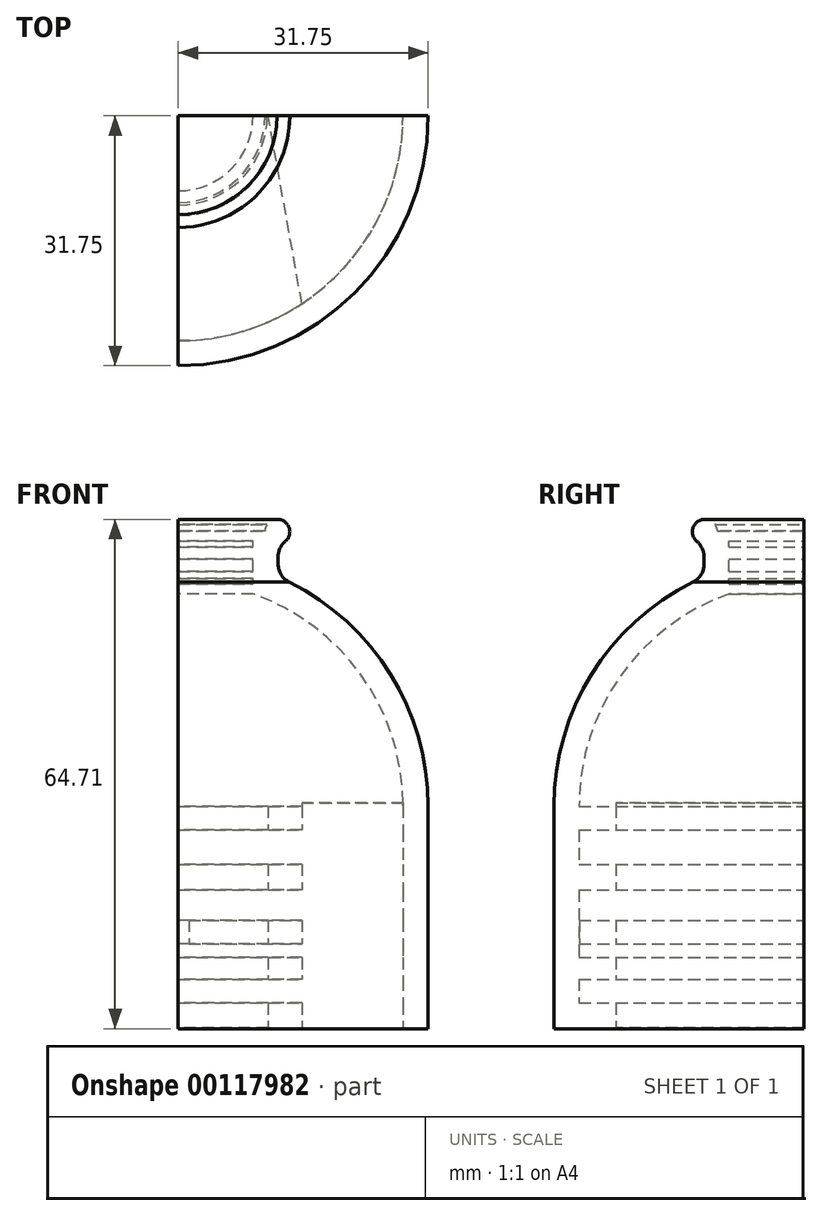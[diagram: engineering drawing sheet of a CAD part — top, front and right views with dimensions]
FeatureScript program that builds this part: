
annotation { "Feature Type Name" : "Feature", "Feature Type Description" : "" }
export const myFeature = defineFeature(function(context is Context, id is Id, definition is map)
    precondition{}
    {
        {
            var Q0;
            Q0=qCreatedBy(makeId("Top.planeOp"),FACE);
            var sketch = newSketch(context, id + "F0", { "sketchPlane" : qUnion([Q0])});
            skCircle(sketch, "E0", {"center": v(0, 0) * mm, "radius": 31.75 * mm});
            skCircle(sketch, "E1", {"center": v(0, 0) * mm, "radius": 28.58 * mm});
            skSolve(sketch);
        }
        {
            var Q0;
            Q0=qSketchRegion(id+"F0",true);
            extrude(context, id + "F1", {"entities" : qUnion([Q0]), "endBound" : BoundingType.SYMMETRIC, "depth" : 50.8 * mm});
        }
        {
            var Q0;
            Q0=makeQuery(id+"F1.opExtrude","CAP_FACE",FACE,{"disambiguationData":[OSD([sQuery(id+"F0.wireOp",EDGE,"E0"),sQuery(id+"F0.wireOp",EDGE,"E1")])],"isStart":false});
            var sketch = newSketch(context, id + "F2", { "sketchPlane" : qUnion([Q0])});
            skArc(sketch, "E2", {"start": v(0, -31.75) * mm, "mid": v(31.75, 0) * mm, "end": v(0, 31.75) * mm});
            skArc(sketch, "E3", {"start": v(0, -28.58) * mm, "mid": v(28.58, 0) * mm, "end": v(0, 28.58) * mm});
            skLineSegment(sketch, "E4", {"start": v(0, 31.75) * mm, "end": v(0, -31.75) * mm, "construction": true});
            skLineSegment(sketch, "E5", {"start": v(0, 31.75) * mm, "end": v(0, 28.58) * mm});
            skLineSegment(sketch, "E6", {"start": v(0, -31.75) * mm, "end": v(0, -28.58) * mm});
            skSolve(sketch);
        }
        {
            var Q0;
            Q0=qSketchRegion(id+"F2",true);
            var Q1;
            Q1=sQuery(id+"F2.wireOp",EDGE,"E4");
            revolve(context, id + "F3", {"operationType" : NewBodyOperationType.ADD, "entities" : qUnion([Q0]), "axis" : qUnion([Q1]), "revolveType" : RevolveType.ONE_DIRECTION, "angle" : 180 * degree});
        }
        {
            var Q0;
            Q0=makeQuery(id+"F1.opExtrude","SWEPT_BODY",BODY,{"disambiguationData":[OSD([sQuery(id+"F0.wireOp",EDGE,"E0"),sQuery(id+"F0.wireOp",EDGE,"E1")])]});
            var Q1;
            Q1=qCreatedBy(makeId("Top.planeOp"),FACE);
            mirror(context, id + "F4", {"operationType" : NewBodyOperationType.ADD, "entities" : qUnion([Q0]), "mirrorPlane" : qUnion([Q1])});
        }
        {
            var Q0;
            Q0=qCreatedBy(makeId("Top.planeOp"),FACE);
            cPlane(context, id + "F5", {"entities" : qUnion([Q0]), "cplaneType" : CPlaneType.OFFSET, "offset" : 57.15 * mm, "width" : 152.4 * mm, "height" : 152.4 * mm});
        }
        {
            var Q0;
            Q0=qCreatedBy(id+"F5.planeOp",FACE);
            var sketch = newSketch(context, id + "F6", { "sketchPlane" : qUnion([Q0])});
            skCircle(sketch, "E7", {"center": v(0, 0) * mm, "radius": 12.7 * mm});
            skSolve(sketch);
        }
        {
            var Q0;
            Q0=qSketchRegion(id+"F6",true);
            extrude(context, id + "F7", {"entities" : qUnion([Q0]), "operationType" : NewBodyOperationType.ADD, "endBound" : BoundingType.SYMMETRIC, "depth" : 6.35 * mm});
        }
        {
            var Q0;
            Q0=qCreatedBy(makeId("Top.planeOp"),FACE);
            cPlane(context, id + "F8", {"entities" : qUnion([Q0]), "cplaneType" : CPlaneType.OFFSET, "offset" : 57.15 * mm, "oppositeDirection" : true, "width" : 152.4 * mm, "height" : 152.4 * mm});
        }
        {
            var Q0;
            Q0=makeQuery(id+"F7.opExtrude","CAP_FACE",FACE,{"disambiguationData":[OSD([sQuery(id+"F6.wireOp",EDGE,"E7")])],"isStart":false});
            var sketch = newSketch(context, id + "F9", { "sketchPlane" : qUnion([Q0])});
            skCircle(sketch, "E8", {"center": v(0, 0) * mm, "radius": 9.53 * mm});
            skSolve(sketch);
        }
        {
            var Q0;
            Q0=qSketchRegion(id+"F9",true);
            extrude(context, id + "F10", {"entities" : qUnion([Q0]), "operationType" : NewBodyOperationType.REMOVE, "oppositeDirection" : true, "depth" : 25.4 * mm});
        }
        {
            var Q0;
            Q0=qCreatedBy(makeId("Front.planeOp"),FACE);
            var sketch = newSketch(context, id + "F11", { "sketchPlane" : qUnion([Q0])});
            skLineSegment(sketch, "E9", {"start": v(0, -57.15) * mm, "end": v(11.6, -79.09) * mm});
            skLineSegment(sketch, "E10", {"start": v(11.6, -79.09) * mm, "end": v(33.29, -79.09) * mm});
            skLineSegment(sketch, "E11", {"start": v(33.29, -79.09) * mm, "end": v(33.29, -57.05) * mm});
            skLineSegment(sketch, "E12", {"start": v(33.29, -57.05) * mm, "end": v(28.2, -40) * mm});
            skPoint(sketch, "E13.orphan", {"position": v(31.75, -25.4) * mm});
            skPoint(sketch, "E14.orphan", {"position": v(-31.75, -25.4) * mm});
            skLineSegment(sketch, "E15", {"start": v(28.2, -40) * mm, "end": v(27.19, -39.19) * mm});
            skArc(sketch, "E16.0", {"start": v(0, -56.61) * mm, "mid": v(14.18, -53.2) * mm, "end": v(25.27, -43.72) * mm});
            skLineSegment(sketch, "E17", {"start": v(27.19, -39.19) * mm, "end": v(25.27, -43.72) * mm});
            skLineSegment(sketch, "E18", {"start": v(0, -56.61) * mm, "end": v(0, -57.15) * mm});
            skSolve(sketch);
        }
        {
            var Q0;
            Q0=qSketchRegion(id+"F11",true);
            extrude(context, id + "F12", {"entities" : qUnion([Q0]), "operationType" : NewBodyOperationType.ADD, "endBound" : BoundingType.SYMMETRIC, "depth" : 3.17 * mm});
        }
        {
            var Q0;
            Q0=qCreatedBy(makeId("Front.planeOp"),FACE);
            var sketch = newSketch(context, id + "F13", { "sketchPlane" : qUnion([Q0])});
            skLineSegment(sketch, "E19", {"start": v(0, 72.95) * mm, "end": v(0, -20.55) * mm, "construction": true});
            skSolve(sketch);
        }
        {
            var Q0;
            Q0=makeQuery(id+"F1.opExtrude","SWEPT_BODY",BODY,{"disambiguationData":[OSD([sQuery(id+"F0.wireOp",EDGE,"E0"),sQuery(id+"F0.wireOp",EDGE,"E1")])]});
            var Q1;
            Q1=sQuery(id+"F13.wireOp",EDGE,"E19");
            circularPattern(context, id + "F14", {"entities" : qUnion([Q0]), "axis" : qUnion([Q1]), "angle" : 90 * degree, "instanceCount" : 4});
        }
        {
            var Q0;
            Q0=qCreatedBy(makeId("Front.planeOp"),FACE);
            var sketch = newSketch(context, id + "F15", { "sketchPlane" : qUnion([Q0])});
            skLineSegment(sketch, "E20", {"start": v(0, 46.85) * mm, "end": v(0, 31.4) * mm, "construction": true});
            skCircle(sketch, "E21", {"center": v(12.6, 60.23) * mm, "radius": 1.59 * mm});
            skSolve(sketch);
        }
        {
            var Q0;
            Q0=qSketchRegion(id+"F15",true);
            var Q1;
            Q1=sQuery(id+"F15.wireOp",EDGE,"E20");
            revolve(context, id + "F16", {"operationType" : NewBodyOperationType.ADD, "entities" : qUnion([Q0]), "axis" : qUnion([Q1]), "revolveType" : RevolveType.FULL});
        }
        {
            var Q0;
            Q0=qCreatedBy(id+"F5.planeOp",FACE);
            var sketch = newSketch(context, id + "F17", { "sketchPlane" : qUnion([Q0])});
            skLineSegment(sketch, "E22", {"start": v(0, -45.12) * mm, "end": v(0, 0) * mm});
            skLineSegment(sketch, "E23", {"start": v(0, 0) * mm, "end": v(39.38, 0) * mm});
            skLineSegment(sketch, "E24", {"start": v(39.38, 0) * mm, "end": v(39.38, 53.9) * mm});
            skLineSegment(sketch, "E25", {"start": v(39.38, 53.9) * mm, "end": v(-55.46, 53.9) * mm});
            skLineSegment(sketch, "E26", {"start": v(-55.46, 53.9) * mm, "end": v(-55.46, -47.21) * mm});
            skLineSegment(sketch, "E27", {"start": v(-55.46, -47.21) * mm, "end": v(0, -45.12) * mm});
            skSolve(sketch);
        }
        {
            var Q0;
            Q0=qSketchRegion(id+"F17",true);
            extrude(context, id + "F18", {"entities" : qUnion([Q0]), "operationType" : NewBodyOperationType.REMOVE, "endBound" : BoundingType.THROUGH_ALL, "oppositeDirection" : true, "depth" : 25.4 * mm, "hasSecondDirection" : true, "secondDirectionOppositeDirection" : false, "secondDirectionDepth" : 25.4 * mm});
        }
        {
            var Q0;
            Q0=qCreatedBy(makeId("Right.planeOp"),FACE);
            var sketch = newSketch(context, id + "F19", { "sketchPlane" : qUnion([Q0])});
            skLineSegment(sketch, "E28.bottom", {"start": v(8.43, -2.89) * mm, "end": v(-42.27, -2.89) * mm});
            skLineSegment(sketch, "E28.top", {"start": v(8.43, -82.1) * mm, "end": v(-42.27, -82.1) * mm});
            skLineSegment(sketch, "E28.left", {"start": v(8.43, -2.89) * mm, "end": v(8.43, -82.1) * mm});
            skLineSegment(sketch, "E28.right", {"start": v(-42.27, -2.89) * mm, "end": v(-42.27, -82.1) * mm});
            skSolve(sketch);
        }
        {
            var Q0;
            Q0=qSketchRegion(id+"F19",true);
            extrude(context, id + "F20", {"entities" : qUnion([Q0]), "operationType" : NewBodyOperationType.REMOVE, "endBound" : BoundingType.THROUGH_ALL, "depth" : 25.4 * mm});
        }
        {
            var Q0;
            Q0=qCreatedBy(makeId("Right.planeOp"),FACE);
            var sketch = newSketch(context, id + "F21", { "sketchPlane" : qUnion([Q0])});
            skLineSegment(sketch, "E29.bottom", {"start": v(-29.08, -2.78) * mm, "end": v(0, -2.78) * mm});
            skLineSegment(sketch, "E29.top", {"start": v(-29.08, 0.4) * mm, "end": v(0, 0.4) * mm});
            skLineSegment(sketch, "E29.left", {"start": v(-29.08, -2.78) * mm, "end": v(-29.08, 0.4) * mm});
            skLineSegment(sketch, "E29.right", {"start": v(0, -2.78) * mm, "end": v(0, 0.4) * mm});
            skLineSegment(sketch, "E30.bottom", {"start": v(-28.67, 25.37) * mm, "end": v(0, 25.37) * mm});
            skLineSegment(sketch, "E30.top", {"start": v(-28.67, 22.34) * mm, "end": v(0, 22.34) * mm});
            skLineSegment(sketch, "E30.left", {"start": v(-28.67, 25.37) * mm, "end": v(-28.67, 22.34) * mm});
            skLineSegment(sketch, "E30.right", {"start": v(0, 25.37) * mm, "end": v(0, 22.34) * mm});
            skLineSegment(sketch, "E31.bottom", {"start": v(-28.67, 18) * mm, "end": v(0, 18) * mm});
            skLineSegment(sketch, "E31.top", {"start": v(-28.67, 14.71) * mm, "end": v(0, 14.71) * mm});
            skLineSegment(sketch, "E31.left", {"start": v(-28.67, 18) * mm, "end": v(-28.67, 14.71) * mm});
            skLineSegment(sketch, "E31.right", {"start": v(0, 18) * mm, "end": v(0, 14.71) * mm});
            skLineSegment(sketch, "E32.bottom", {"start": v(-28.54, 10.9) * mm, "end": v(0, 10.9) * mm});
            skLineSegment(sketch, "E32.top", {"start": v(-28.54, 7.87) * mm, "end": v(0, 7.87) * mm});
            skLineSegment(sketch, "E32.left", {"start": v(-28.54, 10.9) * mm, "end": v(-28.54, 7.87) * mm});
            skLineSegment(sketch, "E32.right", {"start": v(0, 10.9) * mm, "end": v(0, 7.87) * mm});
            skLineSegment(sketch, "E33.bottom", {"start": v(-28.67, 6.16) * mm, "end": v(0, 6.16) * mm});
            skLineSegment(sketch, "E33.top", {"start": v(-28.67, 3.4) * mm, "end": v(0, 3.4) * mm});
            skLineSegment(sketch, "E33.left", {"start": v(-28.67, 6.16) * mm, "end": v(-28.67, 3.4) * mm});
            skLineSegment(sketch, "E33.right", {"start": v(0, 6.16) * mm, "end": v(0, 3.4) * mm});
            skSolve(sketch);
        }
        {
            var Q0;
            Q0 = qSketchRegion(id + "F21", true);
            var Q1;
            Q1=makeQuery(id+"F1.opExtrude","SWEPT_FACE",FACE,{"disambiguationData":[OSD([sQuery(id+"F0.wireOp",EDGE,"E1")])]});
            extrude(context, id + "F22", {"entities" : qUnion([Q0]), "operationType" : NewBodyOperationType.ADD, "endBound" : BoundingType.UP_TO_SURFACE, "endBoundEntityFace" : qUnion([Q1]), "depth" : 25.4 * mm});
        }
        {
            var Q0;
            Q0=makeQuery(id+"F22.boolean.opBoolean","MERGE",FACE,{"derivedFrom":[makeQuery(id+"F18.boolean.opBoolean","COPY",FACE,{"derivedFrom":makeQuery(id+"F18.opExtrude","SWEPT_FACE",FACE,{"disambiguationData":[OSD([sQuery(id+"F17.wireOp",EDGE,"E22")])]})}),makeQuery(id+"F22.opExtrude","CAP_FACE",FACE,{"disambiguationData":[OSD([sQuery(id+"F21.wireOp",EDGE,"E29.bottom"),sQuery(id+"F21.wireOp",EDGE,"E29.top"),sQuery(id+"F21.wireOp",EDGE,"E29.left"),sQuery(id+"F21.wireOp",EDGE,"E29.right")])],"isStart":true}),makeQuery(id+"F22.opExtrude","CAP_FACE",FACE,{"disambiguationData":[OSD([sQuery(id+"F21.wireOp",EDGE,"E30.bottom"),sQuery(id+"F21.wireOp",EDGE,"E30.top"),sQuery(id+"F21.wireOp",EDGE,"E30.left"),sQuery(id+"F21.wireOp",EDGE,"E30.right")])],"isStart":true}),makeQuery(id+"F22.opExtrude","CAP_FACE",FACE,{"disambiguationData":[OSD([sQuery(id+"F21.wireOp",EDGE,"E31.bottom"),sQuery(id+"F21.wireOp",EDGE,"E31.top"),sQuery(id+"F21.wireOp",EDGE,"E31.left"),sQuery(id+"F21.wireOp",EDGE,"E31.right")])],"isStart":true}),makeQuery(id+"F22.opExtrude","CAP_FACE",FACE,{"disambiguationData":[OSD([sQuery(id+"F21.wireOp",EDGE,"E33.bottom"),sQuery(id+"F21.wireOp",EDGE,"E33.top"),sQuery(id+"F21.wireOp",EDGE,"E33.left"),sQuery(id+"F21.wireOp",EDGE,"E33.right")])],"isStart":true})]});
            var sketch = newSketch(context, id + "F23", { "sketchPlane" : qUnion([Q0])});
            skLineSegment(sketch, "E34.bottom", {"start": v(11, 60.33) * mm, "end": v(0, 60.33) * mm});
            skLineSegment(sketch, "E34.top", {"start": v(11, 59.08) * mm, "end": v(0, 59.08) * mm});
            skLineSegment(sketch, "E34.left", {"start": v(11, 60.33) * mm, "end": v(11, 59.08) * mm});
            skLineSegment(sketch, "E34.right", {"start": v(0, 60.33) * mm, "end": v(0, 59.08) * mm});
            skLineSegment(sketch, "E35.bottom", {"start": v(10.47, 58.27) * mm, "end": v(0, 58.27) * mm});
            skLineSegment(sketch, "E35.top", {"start": v(10.47, 56.8) * mm, "end": v(0, 56.8) * mm});
            skLineSegment(sketch, "E35.left", {"start": v(10.47, 58.27) * mm, "end": v(10.47, 56.8) * mm});
            skLineSegment(sketch, "E35.right", {"start": v(0, 58.27) * mm, "end": v(0, 56.8) * mm});
            skLineSegment(sketch, "E36.bottom", {"start": v(10.35, 55.16) * mm, "end": v(0, 55.16) * mm});
            skLineSegment(sketch, "E36.top", {"start": v(10.35, 54.31) * mm, "end": v(0, 54.31) * mm});
            skLineSegment(sketch, "E36.left", {"start": v(10.35, 55.16) * mm, "end": v(10.35, 54.31) * mm});
            skLineSegment(sketch, "E36.right", {"start": v(0, 55.16) * mm, "end": v(0, 54.31) * mm});
            skLineSegment(sketch, "E37.bottom", {"start": v(10.3, 53.6) * mm, "end": v(0, 53.6) * mm});
            skLineSegment(sketch, "E37.top", {"start": v(10.3, 52.34) * mm, "end": v(0, 52.34) * mm});
            skLineSegment(sketch, "E37.left", {"start": v(10.3, 53.6) * mm, "end": v(10.3, 52.34) * mm});
            skLineSegment(sketch, "E37.right", {"start": v(0, 53.6) * mm, "end": v(0, 52.34) * mm});
            skSolve(sketch);
        }
        {
            var Q0;
            Q0 = qSketchRegion(id + "F23", true);
            var Q1;
            Q1=makeQuery(id+"F10.boolean.opBoolean","COPY",FACE,{"derivedFrom":makeQuery(id+"F10.opExtrude","SWEPT_FACE",FACE,{"disambiguationData":[OSD([sQuery(id+"F9.wireOp",EDGE,"E8")])]})});
            extrude(context, id + "F24", {"entities" : qUnion([Q0]), "operationType" : NewBodyOperationType.ADD, "endBound" : BoundingType.UP_TO_SURFACE, "oppositeDirection" : true, "endBoundEntityFace" : qUnion([Q1]), "depth" : 25.4 * mm});
        }
        {
            var Q0;
            Q0=makeQuery(id+"F22.opExtrude","SWEPT_FACE",FACE,{"disambiguationData":[OSD([sQuery(id+"F21.wireOp",EDGE,"E29.bottom")])]});
            var sketch = newSketch(context, id + "F25", { "sketchPlane" : qUnion([Q0])});
            skLineSegment(sketch, "E38.bottom", {"start": v(11.43, 0) * mm, "end": v(28.58, 0) * mm});
            skLineSegment(sketch, "E38.left", {"start": v(11.43, 0) * mm, "end": v(15.72, 23.86) * mm});
            skArc(sketch, "E39.0", {"start": v(28.58, 0) * mm, "mid": v(25.16, 13.55) * mm, "end": v(15.72, 23.86) * mm});
            skPoint(sketch, "E40.orphan", {"position": v(0, 28.58) * mm});
            skSolve(sketch);
        }
        {
            var Q0;
            Q0 = qSketchRegion(id + "F25", true);
            extrude(context, id + "F26", {"entities" : qUnion([Q0]), "operationType" : NewBodyOperationType.REMOVE, "oppositeDirection" : true, "depth" : 28.57 * mm});
        }
        {
            var Q0;
            Q0=makeQuery(id+"F7.boolean.opBoolean","INTERSECT",EDGE,{"derivedFrom":[makeQuery(id+"F3.opRevolve","SWEPT_FACE",FACE,{"disambiguationData":[OSD([sQuery(id+"F2.wireOp",EDGE,"E2")])]}),makeQuery(id+"F7.opExtrude","SWEPT_FACE",FACE,{"disambiguationData":[OSD([sQuery(id+"F6.wireOp",EDGE,"E7")])]})]});
            var Q1;
            {var subQ0=makeQuery(id+"F7.opExtrude","SWEPT_FACE",FACE,{"disambiguationData":[OSD([sQuery(id+"F6.wireOp",EDGE,"E7")])]});Q1=makeQuery(id+"F16.boolean.opBoolean","INTERSECT",EDGE,{"derivedFrom":[subQ0,makeQuery(id+"F14.opPattern","COPY",FACE,{"derivedFrom":subQ0,"instanceName":"1"}),makeQuery(id+"F14.opPattern","COPY",FACE,{"derivedFrom":subQ0,"instanceName":"2"}),makeQuery(id+"F14.opPattern","COPY",FACE,{"derivedFrom":subQ0,"instanceName":"3"}),makeQuery(id+"F16.opRevolve","SWEPT_FACE",FACE,{"disambiguationData":[OSD([sQuery(id+"F15.wireOp",EDGE,"E21")])]})]});}
            fillet(context, id + "F27", {"entities" : qUnion([Q0, Q1]), "radius" : 2.54 * mm, "tangentPropagation" : true, "allowEdgeOverflow" : false});
        }
        {
            var Q0;
            {var subQ0=sQuery(id+"F23.wireOp",EDGE,"E36.right");var subQ5=sQuery(id+"F23.wireOp",EDGE,"E34.right");var subQ7=sQuery(id+"F23.wireOp",EDGE,"E37.right");var subQ9=sQuery(id+"F21.wireOp",EDGE,"E33.right");var subQ10=sQuery(id+"F21.wireOp",EDGE,"E31.right");var subQ11=sQuery(id+"F21.wireOp",EDGE,"E30.right");var subQ12=sQuery(id+"F23.wireOp",EDGE,"E35.right");var subQ15=sQuery(id+"F21.wireOp",EDGE,"E29.right");Q0=makeQuery(id+"F26.boolean.opBoolean","SPLIT",FACE,{"disambiguationData":[TD([makeQuery(id+"F1.opExtrude","SWEPT_FACE",FACE,{"disambiguationData":[OSD([sQuery(id+"F0.wireOp",EDGE,"E0")])]})])],"derivedFrom":makeQuery(id+"F24.boolean.opBoolean","MERGE",FACE,{"derivedFrom":[makeQuery(id+"F22.boolean.opBoolean","MERGE",FACE,{"derivedFrom":[makeQuery(id+"F18.boolean.opBoolean","COPY",FACE,{"derivedFrom":makeQuery(id+"F18.opExtrude","SWEPT_FACE",FACE,{"disambiguationData":[OSD([sQuery(id+"F17.wireOp",EDGE,"E23")])]})}),makeQuery(id+"F22.opExtrude","SWEPT_FACE",FACE,{"disambiguationData":[OSD([subQ15])]}),makeQuery(id+"F22.opExtrude","SWEPT_FACE",FACE,{"disambiguationData":[OSD([subQ11])]}),makeQuery(id+"F22.opExtrude","SWEPT_FACE",FACE,{"disambiguationData":[OSD([subQ10])]}),makeQuery(id+"F22.opExtrude","SWEPT_FACE",FACE,{"disambiguationData":[OSD([sQuery(id+"F21.wireOp",EDGE,"E32.right")])]}),makeQuery(id+"F22.opExtrude","SWEPT_FACE",FACE,{"disambiguationData":[OSD([subQ9])]})]}),makeQuery(id+"F24.opExtrude","SWEPT_FACE",FACE,{"disambiguationData":[OSD([subQ5])]}),makeQuery(id+"F24.opExtrude","SWEPT_FACE",FACE,{"disambiguationData":[OSD([subQ12])]}),makeQuery(id+"F24.opExtrude","SWEPT_FACE",FACE,{"disambiguationData":[OSD([subQ0])]}),makeQuery(id+"F24.opExtrude","SWEPT_FACE",FACE,{"disambiguationData":[OSD([subQ7])]})]})});}
            var sketch = newSketch(context, id + "F28", { "sketchPlane" : qUnion([Q0])});
            skLineSegment(sketch, "E41.bottom", {"start": v(-12.62, 61.82) * mm, "end": v(0, 61.82) * mm});
            skLineSegment(sketch, "E41.top", {"start": v(-12.62, 61.17) * mm, "end": v(0, 61.17) * mm});
            skLineSegment(sketch, "E41.left", {"start": v(-12.62, 61.82) * mm, "end": v(-12.62, 61.17) * mm});
            skLineSegment(sketch, "E41.right", {"start": v(0, 61.82) * mm, "end": v(0, 61.17) * mm});
            skSolve(sketch);
        }
        {
            var Q0;
            Q0 = qSketchRegion(id + "F28", true);
            var Q1;
            Q1=makeQuery(id+"F16.opRevolve","SWEPT_FACE",FACE,{"disambiguationData":[OSD([sQuery(id+"F15.wireOp",EDGE,"E21")])]});
            extrude(context, id + "F29", {"entities" : qUnion([Q0]), "operationType" : NewBodyOperationType.ADD, "endBound" : BoundingType.UP_TO_SURFACE, "oppositeDirection" : true, "endBoundEntityFace" : qUnion([Q1]), "depth" : 25.4 * mm});
        }
    });
